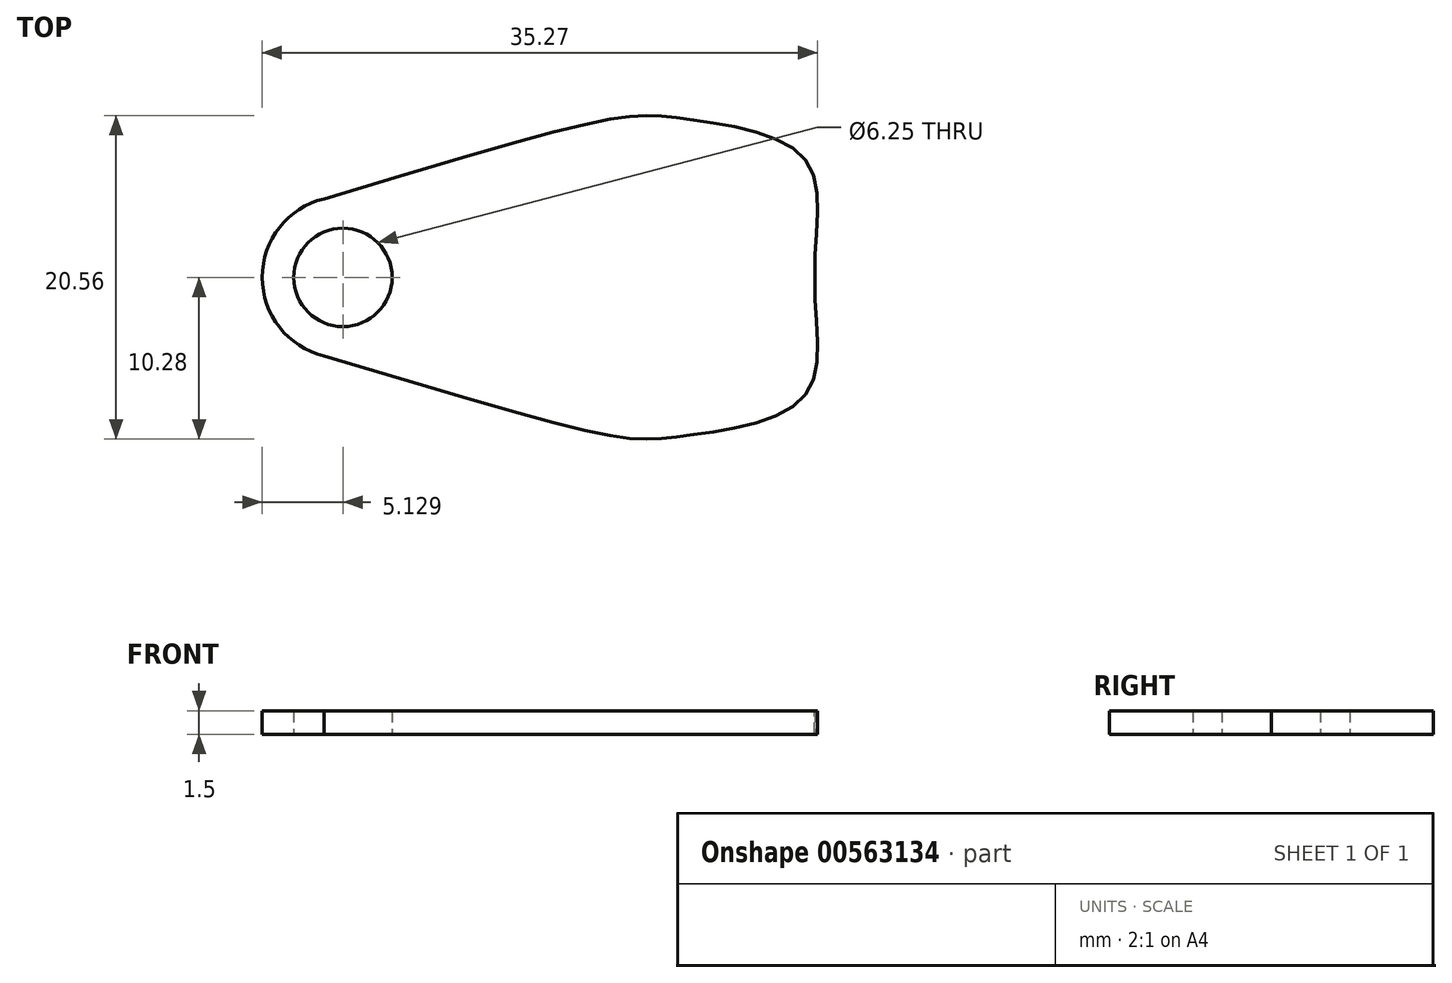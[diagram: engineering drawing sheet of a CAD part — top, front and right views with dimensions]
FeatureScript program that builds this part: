
annotation { "Feature Type Name" : "Feature", "Feature Type Description" : "" }
export const myFeature = defineFeature(function(context is Context, id is Id, definition is map)
    precondition{}
    {
        {
            var Q0;
            Q0=qCreatedBy(makeId("Top.planeOp"),FACE);
            var sketch = newSketch(context, id + "F0", { "sketchPlane" : qUnion([Q0])});
            skFitSpline(sketch, "E0", {"points": [v(-15.74, 4.98) * mm, v(7.48, 10.03) * mm, v(14.8, 7.5) * mm, v(15.43, 0) * mm], "startDerivative": vector(121.96, 36.63) * mm, "endDerivative": vector(0.84, -32.13) * mm});
            skFitSpline(sketch, "E1.MirrorCS", {"points": [v(-15.74, -4.98) * mm, v(7.48, -10.03) * mm, v(14.8, -7.5) * mm, v(15.43, 0) * mm], "startDerivative": vector(121.96, -36.63) * mm, "endDerivative": vector(0.84, 32.13) * mm});
            skArc(sketch, "E2", {"start": v(-15.74, 4.98) * mm, "mid": v(-19.67, 0) * mm, "end": v(-15.74, -4.98) * mm});
            skCircle(sketch, "E3", {"center": v(-14.54, 0) * mm, "radius": 3.13 * mm});
            skSolve(sketch);
        }
        {
            var Q0;
            Q0 = qSketchRegion(id + "F0", true);
            extrude(context, id + "F1", {"entities" : qUnion([Q0]), "depth" : 1.5 * mm, "offsetDistance" : 25 * mm});
        }
    });
